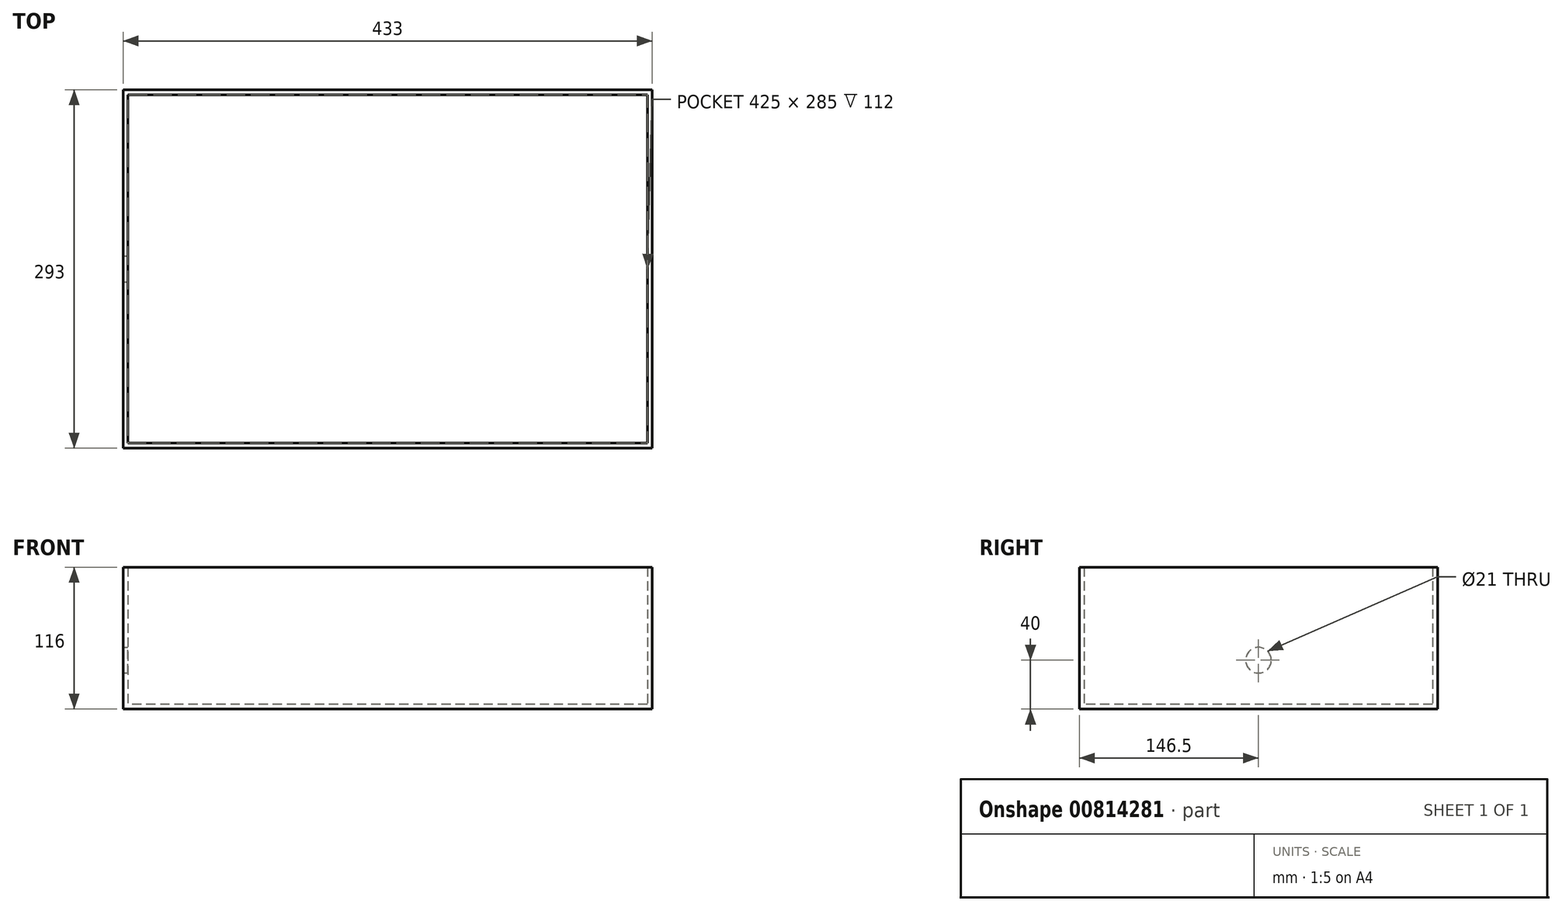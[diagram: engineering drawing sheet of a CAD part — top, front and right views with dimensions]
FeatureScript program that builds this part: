
annotation { "Feature Type Name" : "Feature", "Feature Type Description" : "" }
export const myFeature = defineFeature(function(context is Context, id is Id, definition is map)
    precondition{}
    {
        {
            var Q0;
            Q0=qCreatedBy(makeId("Top.planeOp"),FACE);
            var sketch = newSketch(context, id + "F0", { "sketchPlane" : qUnion([Q0])});
            skLineSegment(sketch, "E0.bottom", {"start": v(216.5, 146.5) * mm, "end": v(-216.5, 146.5) * mm});
            skLineSegment(sketch, "E0.top", {"start": v(216.5, -146.5) * mm, "end": v(-216.5, -146.5) * mm});
            skLineSegment(sketch, "E0.left", {"start": v(216.5, 146.5) * mm, "end": v(216.5, -146.5) * mm});
            skLineSegment(sketch, "E0.right", {"start": v(-216.5, 146.5) * mm, "end": v(-216.5, -146.5) * mm});
            skPoint(sketch, "E0.middle", {"position": v(0, 0) * mm});
            skSolve(sketch);
        }
        {
            var Q0;
            Q0 = qSketchRegion(id + "F0", true);
            extrude(context, id + "F1", {"entities" : qUnion([Q0]), "depth" : 116 * mm, "offsetDistance" : 25 * mm});
        }
        {
            var Q0;
            Q0=makeQuery(id+"F1.opExtrude","CAP_FACE",FACE,{"disambiguationData":[OSD([sQuery(id+"F0.wireOp",EDGE,"E0.bottom"),sQuery(id+"F0.wireOp",EDGE,"E0.top"),sQuery(id+"F0.wireOp",EDGE,"E0.left"),sQuery(id+"F0.wireOp",EDGE,"E0.right")])],"isStart":false});
            shell(context, id + "F2", {"entities" : qUnion([Q0]), "thickness" : 4 * mm});
        }
        {
            var Q0;
            Q0=makeQuery(id+"F1.opExtrude","SWEPT_FACE",FACE,{"disambiguationData":[OSD([sQuery(id+"F0.wireOp",EDGE,"E0.right")])]});
            var sketch = newSketch(context, id + "F3", { "sketchPlane" : qUnion([Q0])});
            skLineSegment(sketch, "E1", {"start": v(-146.5, 40) * mm, "end": v(146.5, 40) * mm, "construction": true});
            skPoint(sketch, "E2", {"position": v(0, 40) * mm});
            skSolve(sketch);
        }
        {
            var Q0;
            Q0=sQuery(id+"F3.wireOp",VERTEX,"E2");
            var Q1;
            Q1=makeQuery(id+"F1.opExtrude","SWEPT_BODY",BODY,{"disambiguationData":[OSD([sQuery(id+"F0.wireOp",EDGE,"E0.bottom"),sQuery(id+"F0.wireOp",EDGE,"E0.top"),sQuery(id+"F0.wireOp",EDGE,"E0.left"),sQuery(id+"F0.wireOp",EDGE,"E0.right")])]});
            hole(context, id + "F4", {"style" : HoleStyle.SIMPLE, "endStyle" : HoleEndStyle.BLIND, "holeDiameter" : 21 * mm, "majorDiameter" : 5 * mm, "holeDepth" : 5 * mm, "isTappedThrough" : true, "tappedDepth" : 12 * mm, "tapClearance" : 3, "locations" : qUnion([Q0]), "scope" : qUnion([Q1]), "startStyle" : HoleStartStyle.SKETCH});
        }
    });
